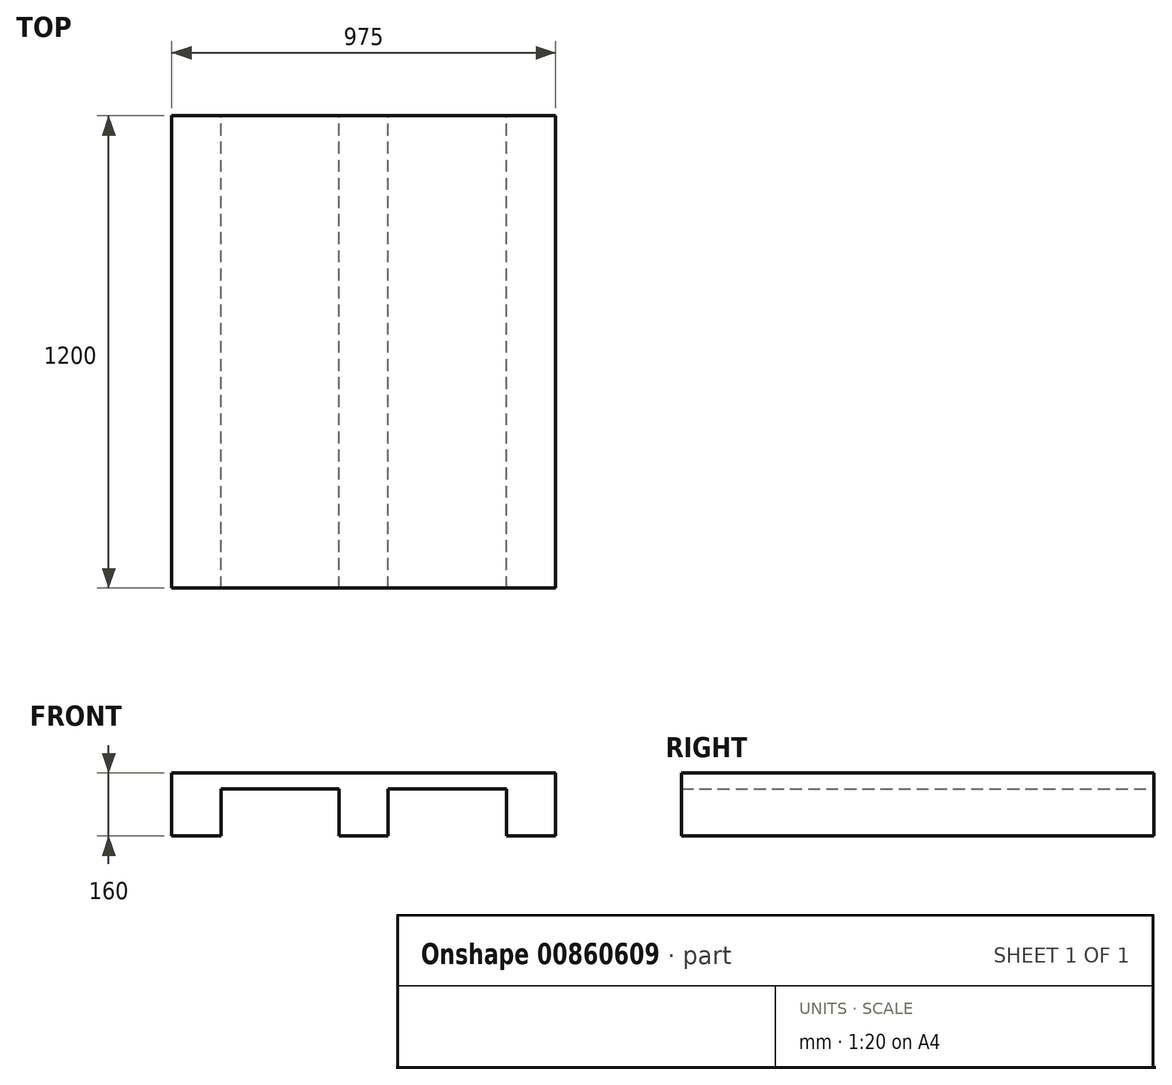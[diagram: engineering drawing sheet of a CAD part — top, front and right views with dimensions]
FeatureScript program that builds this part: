
annotation { "Feature Type Name" : "Feature", "Feature Type Description" : "" }
export const myFeature = defineFeature(function(context is Context, id is Id, definition is map)
    precondition{}
    {
        {
            var Q0;
            Q0=qCreatedBy(makeId("Front.planeOp"),FACE);
            var sketch = newSketch(context, id + "F0", { "sketchPlane" : qUnion([Q0])});
            skLineSegment(sketch, "E0", {"start": v(-487.5, 80) * mm, "end": v(-487.5, -80) * mm});
            skLineSegment(sketch, "E1", {"start": v(-487.5, -80) * mm, "end": v(-362.5, -80) * mm});
            skLineSegment(sketch, "E2", {"start": v(-362.5, -80) * mm, "end": v(-362.5, 40) * mm});
            skLineSegment(sketch, "E3", {"start": v(-362.5, 40) * mm, "end": v(-62.5, 40) * mm});
            skLineSegment(sketch, "E4", {"start": v(-62.5, 40) * mm, "end": v(-62.5, -80) * mm});
            skLineSegment(sketch, "E5", {"start": v(-62.5, -80) * mm, "end": v(62.5, -80) * mm});
            skLineSegment(sketch, "E6", {"start": v(62.5, -80) * mm, "end": v(62.5, 40) * mm});
            skLineSegment(sketch, "E7", {"start": v(62.5, 40) * mm, "end": v(362.5, 40) * mm});
            skLineSegment(sketch, "E8", {"start": v(362.5, 40) * mm, "end": v(362.5, -80) * mm});
            skLineSegment(sketch, "E9", {"start": v(362.5, -80) * mm, "end": v(487.5, -80) * mm});
            skLineSegment(sketch, "E10", {"start": v(487.5, -80) * mm, "end": v(487.5, 80) * mm});
            skLineSegment(sketch, "E11", {"start": v(487.5, 80) * mm, "end": v(-487.5, 80) * mm});
            skLineSegment(sketch, "E12", {"start": v(0, 360.35) * mm, "end": v(0, -307.6) * mm, "construction": true});
            skLineSegment(sketch, "E13", {"start": v(-482.14, 0) * mm, "end": v(832.48, 0) * mm, "construction": true});
            skSolve(sketch);
        }
        {
            var Q0;
            Q0 = qSketchRegion(id + "F0", true);
            extrude(context, id + "F1", {"entities" : qUnion([Q0]), "depth" : 1200 * mm, "offsetDistance" : 25.4 * mm});
        }
    });
